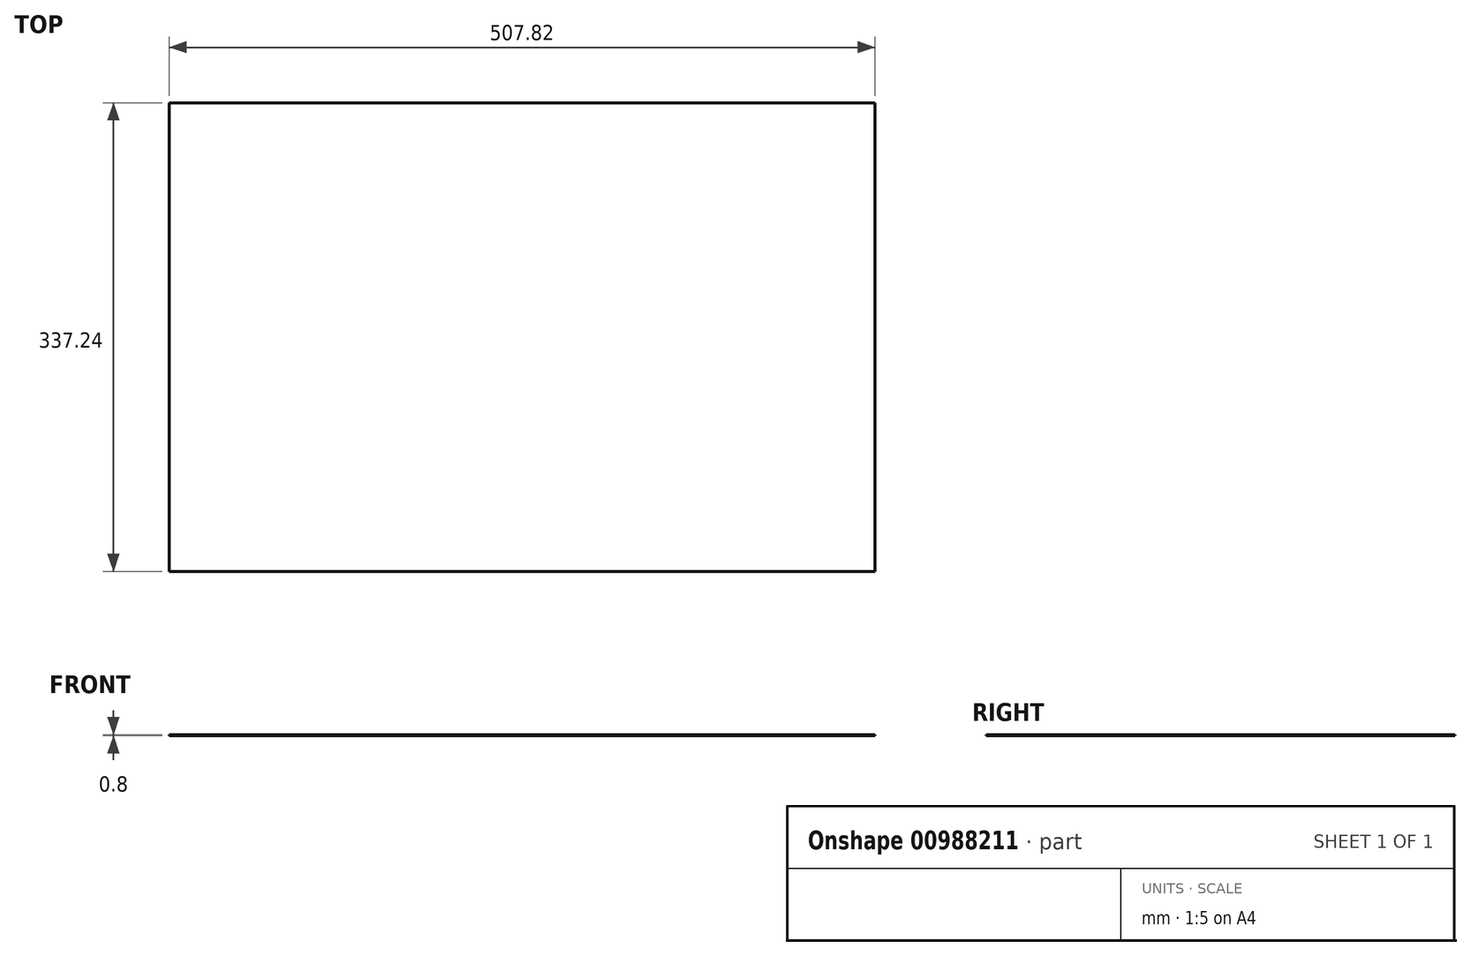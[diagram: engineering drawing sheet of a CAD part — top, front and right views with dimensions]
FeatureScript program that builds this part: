
annotation { "Feature Type Name" : "Feature", "Feature Type Description" : "" }
export const myFeature = defineFeature(function(context is Context, id is Id, definition is map)
    precondition{}
    {
        {
            var Q0;
            Q0=qCreatedBy(makeId("Top.planeOp"),FACE);
            var sketch = newSketch(context, id + "F0", { "sketchPlane" : qUnion([Q0])});
            skLineSegment(sketch, "E0.bottom", {"start": v(0, 0) * mm, "end": v(507.82, 0) * mm});
            skLineSegment(sketch, "E0.top", {"start": v(0, -337.24) * mm, "end": v(507.82, -337.24) * mm});
            skLineSegment(sketch, "E0.left", {"start": v(0, 0) * mm, "end": v(0, -337.24) * mm});
            skLineSegment(sketch, "E0.right", {"start": v(507.82, 0) * mm, "end": v(507.82, -337.24) * mm});
            skSolve(sketch);
        }
        {
            var Q0;
            Q0 = qSketchRegion(id + "F0", true);
            extrude(context, id + "F1", {"entities" : qUnion([Q0]), "endBound" : BoundingType.SYMMETRIC, "depth" : 0.8 * mm, "offsetDistance" : 25.4 * mm});
        }
    });
